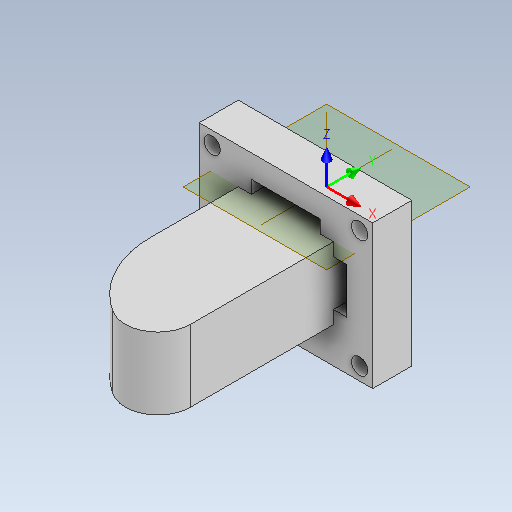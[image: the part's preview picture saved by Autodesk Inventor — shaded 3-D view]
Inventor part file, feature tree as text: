
AUTODESK INVENTOR PART (.ipt)
format: ipt  version: 2025.2 (Build 292293000, 293)  size: 385,024 bytes
history: native  units: mm
features: sketch x8, other x8, extrude x6, fillet x2, plane x1, hole x1
ambient origin geometry x8: Origin, YZ Plane, XZ Plane, XY Plane, X Axis, Y Axis, Z Axis, Center Point
bodies: Body1 (feature_tree)
feature tree (26):
  sketch  "Skizze1"  dims[d2=0.0mm d3=0.0mm d4=0.0mm d5=0.0mm d6=0.0mm d7=0.0mm d8=14.6mm d16=0.0mm d17=11.0mm]
  other  "BKS1"
  plane  "Arbeitsebene1"
  extrude  "Extrusion4"  Depth=14.6mm TaperAngle=0.0deg
  extrude  "Extrusion5"  Depth=5.0mm
  extrude  "Extrusion6"  Depth=6.0mm TaperAngle=0.0deg
  extrude  "Extrusion7"  Depth=22.0mm
  extrude  "Extrusion8"  Depth=5.5mm
  hole  "Bohrung1"  [1 undecoded]
  sketch  "Skizze5"  dims[d28=28.5mm d31=6.0mm d32=0.0mm]
  sketch  "Skizze6"  dims[d33=26.6mm d34=22.0mm]
  sketch  "Skizze7"  dims[d36=5.5mm d38=5.5mm]
  sketch  "Skizze8"  dims[d39=6.0mm d40=6.0mm]
  sketch  "Skizze9"  dims[d41=10.0mm d42=0.0mm d43=10.0mm d44=0.0mm d46=10.0mm d47=0.0mm d48=10.0mm d49=0.0mm]
  sketch  "Skizze10"  dims[d50=2.0mm d51=0.0mm d54=2.0mm d55=2.0mm d56=2.0mm d57=2.0mm d58=2.0mm d60=2.0mm d61=2.0mm d62=2.0mm d63=2.0mm d64=2.0mm d65=2.0mm d66=2.5mm d67=6.0mm d68=4.0mm d69=2.0mm d70=90.0deg d71=2.5mm d72=0.0mm d73=2.0mm d74=2.0mm d75=2.0mm d76=2.0mm d77=2.0mm d78=2.0mm d79=2.0mm d80=2.0mm d81=0.5mm d82=0.872665mm d83=0.5mm d84=0.872665mm]
  other  "BKS1: YZ-Ebene"
  other  "BKS1: XZ-Ebene"
  other  "BKS1: XY-Ebene"
  other  "BKS1: X-Achse"
  other  "BKS1: Y-Achse"
  other  "BKS1: Z-Achse"
  other  "BKS1: Mittelpunkt"
  sketch  "Skizze3"  dims[d18=15.0mm d26=5.0mm]
  extrude  "Extrusion2"  Depth=10.0mm TaperAngle=0.0deg
  fillet  "Rundung2"  Radius=10.0mm
  fillet  "Rundung1"  Radius=10.0mm
note: 1 required parameter value undecoded (feature->parameter linkage not recoverable at this tier; creation-order binding heuristic only, values carry confidence <= 0.55)
